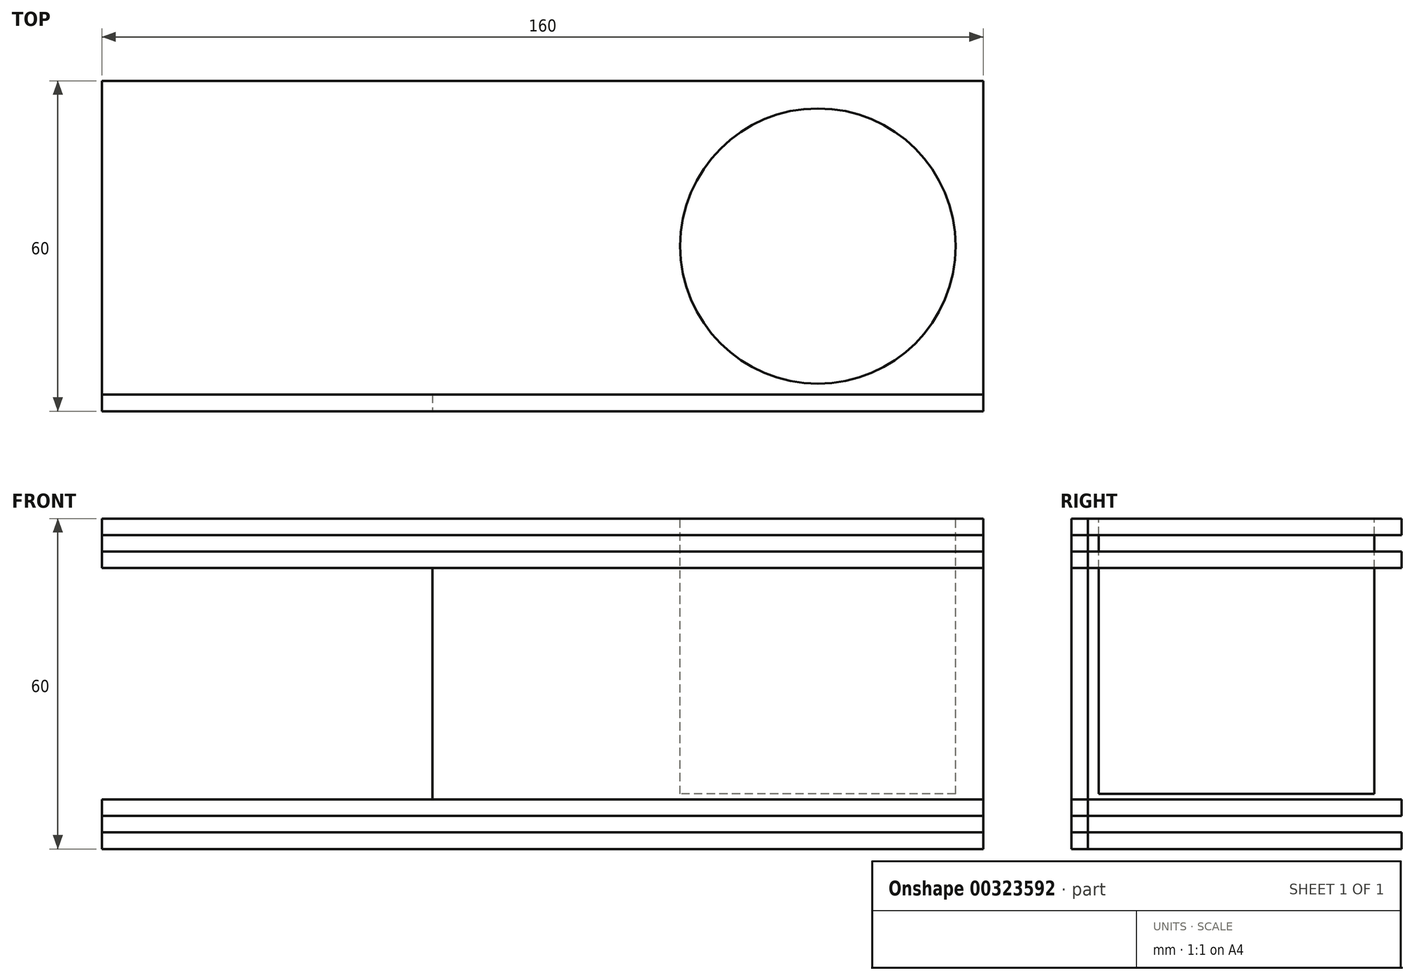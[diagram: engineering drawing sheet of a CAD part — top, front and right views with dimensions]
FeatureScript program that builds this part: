
annotation { "Feature Type Name" : "Feature", "Feature Type Description" : "" }
export const myFeature = defineFeature(function(context is Context, id is Id, definition is map)
    precondition{}
    {
        {
            assignVariable(context, id + "F0", {"name" : "WT", "anyValue" : 3});
        }
        {
            assignVariable(context, id + "F1", {"name" : "BS", "anyValue" : 60});
        }
        {
            assignVariable(context, id + "F2", {"name" : "Rig", "anyValue" : 100});
        }
        {
            var Q0;
            Q0=qCreatedBy(makeId("Top.planeOp"),FACE);
            var sketch = newSketch(context, id + "F3", { "sketchPlane" : qUnion([Q0])});
            skLineSegment(sketch, "E0.bottom", {"start": v(-30, 30) * mm, "end": v(30, 30) * mm});
            skLineSegment(sketch, "E0.top", {"start": v(-30, -30) * mm, "end": v(30, -30) * mm});
            skLineSegment(sketch, "E0.left", {"start": v(-30, 30) * mm, "end": v(-30, -30) * mm});
            skLineSegment(sketch, "E0.right", {"start": v(30, 30) * mm, "end": v(30, -30) * mm});
            skPoint(sketch, "E0.middle", {"position": v(0, 0) * mm});
            skLineSegment(sketch, "E1.bottom", {"start": v(-30, 30) * mm, "end": v(130, 30) * mm});
            skLineSegment(sketch, "E1.top", {"start": v(-30, -30) * mm, "end": v(130, -30) * mm});
            skLineSegment(sketch, "E1.right", {"start": v(130, 30) * mm, "end": v(130, -30) * mm});
            skLineSegment(sketch, "E2", {"start": v(-30, 30) * mm, "end": v(130, -30) * mm, "construction": true});
            skLineSegment(sketch, "E3", {"start": v(50, 0) * mm, "end": v(-30, 0) * mm, "construction": true});
            skPoint(sketch, "E3.endSnap0", {"position": v(-30, 0) * mm});
            skLineSegment(sketch, "E4", {"start": v(50, 0) * mm, "end": v(130, 0) * mm, "construction": true});
            skCircle(sketch, "E5", {"center": v(100, 0) * mm, "radius": 25 * mm});
            skLineSegment(sketch, "E6", {"start": v(130, 27) * mm, "end": v(30, 27) * mm});
            skLineSegment(sketch, "E7.MirrorCS", {"start": v(130, -27) * mm, "end": v(30, -27) * mm});
            skLineSegment(sketch, "E8", {"start": v(33, -27) * mm, "end": v(33, 27) * mm});
            skLineSegment(sketch, "E9", {"start": v(127, 27) * mm, "end": v(127, -27) * mm});
            skLineSegment(sketch, "E10", {"start": v(-27, 0) * mm, "end": v(-27, 27) * mm});
            skLineSegment(sketch, "E11", {"start": v(-27, 27) * mm, "end": v(27, 27) * mm});
            skLineSegment(sketch, "E12", {"start": v(27, 27) * mm, "end": v(27, 0) * mm});
            skLineSegment(sketch, "E13.MirrorCS", {"start": v(-27, 0) * mm, "end": v(-27, -27) * mm});
            skLineSegment(sketch, "E14.MirrorCS", {"start": v(-27, -27) * mm, "end": v(27, -27) * mm});
            skLineSegment(sketch, "E15.MirrorCS", {"start": v(27, -27) * mm, "end": v(27, 0) * mm});
            skSolve(sketch);
        }
        {
            var Q0;
            Q0=sQuery(id+"F3.wireOp",EDGE,"E1.right");
            cPlane(context, id + "F4", {"entities" : qUnion([Q0]), "cplaneType" : CPlaneType.LINE_ANGLE, "offset" : 25 * mm, "angle" : 90 * degree, "width" : 150 * mm, "height" : 150 * mm});
        }
        {
            var Q0;
            Q0=qCreatedBy(id+"F4.planeOp",FACE);
            var sketch = newSketch(context, id + "F5", { "sketchPlane" : qUnion([Q0])});
            skLineSegment(sketch, "E16.0", {"start": v(30, 0) * mm, "end": v(-30, 0) * mm});
            skLineSegment(sketch, "E17", {"start": v(-30, 0) * mm, "end": v(-30, -60) * mm});
            skLineSegment(sketch, "E18", {"start": v(-30, -60) * mm, "end": v(30, -60) * mm});
            skLineSegment(sketch, "E19", {"start": v(30, -60) * mm, "end": v(30, 0) * mm});
            skSolve(sketch);
        }
        {
            var Q0;
            Q0=sQuery(id+"F3.wireOp",EDGE,"E0.right");
            cPlane(context, id + "F6", {"entities" : qUnion([Q0]), "cplaneType" : CPlaneType.LINE_ANGLE, "offset" : 25 * mm, "angle" : 90 * degree, "width" : 150 * mm, "height" : 150 * mm});
        }
        {
            var Q0;
            Q0=qCreatedBy(id+"F6.planeOp",FACE);
            var sketch = newSketch(context, id + "F7", { "sketchPlane" : qUnion([Q0])});
            skLineSegment(sketch, "E20.0", {"start": v(30, 0) * mm, "end": v(-30, 0) * mm});
            skLineSegment(sketch, "E21.bottom", {"start": v(-30, -9) * mm, "end": v(30, -9) * mm});
            skLineSegment(sketch, "E21.top", {"start": v(-30, 0) * mm, "end": v(30, 0) * mm});
            skLineSegment(sketch, "E21.left", {"start": v(-30, -9) * mm, "end": v(-30, 0) * mm});
            skLineSegment(sketch, "E21.right", {"start": v(30, -9) * mm, "end": v(30, 0) * mm});
            skPoint(sketch, "E21.middle", {"position": v(0, -4.5) * mm});
            skLineSegment(sketch, "E22.bottom", {"start": v(-27, -3) * mm, "end": v(27, -3) * mm});
            skLineSegment(sketch, "E22.top", {"start": v(-27, -6) * mm, "end": v(27, -6) * mm});
            skLineSegment(sketch, "E22.left", {"start": v(-27, -3) * mm, "end": v(-27, -6) * mm});
            skLineSegment(sketch, "E22.right", {"start": v(27, -3) * mm, "end": v(27, -6) * mm});
            skLineSegment(sketch, "E23.0", {"start": v(-30, 0) * mm, "end": v(-30, -60) * mm});
            skLineSegment(sketch, "E24.0", {"start": v(-30, -60) * mm, "end": v(30, -60) * mm});
            skLineSegment(sketch, "E25", {"start": v(30, -60) * mm, "end": v(-30, 0) * mm, "construction": true});
            skLineSegment(sketch, "E26", {"start": v(0, -30) * mm, "end": v(-30, -30) * mm, "construction": true});
            skLineSegment(sketch, "E27.MirrorCS", {"start": v(-30, -51) * mm, "end": v(30, -51) * mm});
            skLineSegment(sketch, "E28.MirrorCS", {"start": v(-27, -54) * mm, "end": v(27, -54) * mm});
            skLineSegment(sketch, "E29.MirrorCS", {"start": v(-27, -57) * mm, "end": v(27, -57) * mm});
            skLineSegment(sketch, "E30.MirrorCS", {"start": v(-27, -57) * mm, "end": v(-27, -54) * mm});
            skLineSegment(sketch, "E31.MirrorCS", {"start": v(27, -57) * mm, "end": v(27, -54) * mm});
            skLineSegment(sketch, "E32.MirrorCS", {"start": v(30, -51) * mm, "end": v(30, -60) * mm});
            skLineSegment(sketch, "E33.0", {"start": v(30, -60) * mm, "end": v(30, 0) * mm});
            skLineSegment(sketch, "E34", {"start": v(-27, 0) * mm, "end": v(-27, -60) * mm});
            skLineSegment(sketch, "E35", {"start": v(27, 0) * mm, "end": v(27, -60) * mm});
            skLineSegment(sketch, "E36", {"start": v(27, -6) * mm, "end": v(30, -6) * mm});
            skPoint(sketch, "E36.endSnap0", {"position": v(30, -4.5) * mm});
            skLineSegment(sketch, "E37", {"start": v(-27, -6) * mm, "end": v(-30, -6) * mm});
            skLineSegment(sketch, "E38", {"start": v(27, -54) * mm, "end": v(30, -54) * mm});
            skLineSegment(sketch, "E39", {"start": v(-27, -54) * mm, "end": v(-30, -54) * mm});
            skLineSegment(sketch, "E40", {"start": v(-27, -57) * mm, "end": v(-30, -57) * mm});
            skLineSegment(sketch, "E41", {"start": v(27, -57) * mm, "end": v(30, -57) * mm});
            skSolve(sketch);
        }
        {
            var Q0;
            Q0=qCreatedBy(id+"F6.planeOp",FACE);
            var sketch = newSketch(context, id + "F8", { "sketchPlane" : qUnion([Q0])});
            skLineSegment(sketch, "E42.0", {"start": v(-30, 0) * mm, "end": v(-30, -60) * mm});
            skLineSegment(sketch, "E42.1", {"start": v(-30, 0) * mm, "end": v(30, 0) * mm});
            skLineSegment(sketch, "E42.2", {"start": v(30, -60) * mm, "end": v(30, 0) * mm});
            skLineSegment(sketch, "E42.3", {"start": v(-30, -60) * mm, "end": v(30, -60) * mm});
            skLineSegment(sketch, "E42.4", {"start": v(-27, -6) * mm, "end": v(27, -6) * mm});
            skLineSegment(sketch, "E42.5", {"start": v(-27, -3) * mm, "end": v(27, -3) * mm});
            skLineSegment(sketch, "E42.6", {"start": v(-27, -54) * mm, "end": v(27, -54) * mm});
            skLineSegment(sketch, "E42.7", {"start": v(-27, -57) * mm, "end": v(27, -57) * mm});
            skLineSegment(sketch, "E43", {"start": v(-27, -57) * mm, "end": v(-27, -54) * mm});
            skLineSegment(sketch, "E44", {"start": v(27, -57) * mm, "end": v(27, -54) * mm});
            skLineSegment(sketch, "E45", {"start": v(27, -6) * mm, "end": v(27, -3) * mm});
            skLineSegment(sketch, "E46", {"start": v(-27, -6) * mm, "end": v(-27, -3) * mm});
            skSolve(sketch);
        }
        {
            var Q0;
            Q0=qCreatedBy(makeId("Top.planeOp"),FACE);
            var sketch = newSketch(context, id + "F9", { "sketchPlane" : qUnion([Q0])});
            skLineSegment(sketch, "E47.0", {"start": v(-30, 30) * mm, "end": v(-30, -30) * mm});
            skLineSegment(sketch, "E48.0", {"start": v(-30, -30) * mm, "end": v(130, -30) * mm});
            skLineSegment(sketch, "E49.0", {"start": v(-30, 30) * mm, "end": v(130, 30) * mm});
            skLineSegment(sketch, "E50.0", {"start": v(130, 30) * mm, "end": v(130, -30) * mm});
            skSolve(sketch);
        }
        {
            var Q0;
            Q0=sQuery(id+"F3.wireOp",EDGE,"E1.top");
            cPlane(context, id + "F10", {"entities" : qUnion([Q0]), "cplaneType" : CPlaneType.LINE_ANGLE, "offset" : 25 * mm, "angle" : 0 * degree, "width" : 150 * mm, "height" : 150 * mm});
        }
        {
            var Q0;
            Q0=qCreatedBy(id+"F10.planeOp",FACE);
            var sketch = newSketch(context, id + "F11", { "sketchPlane" : qUnion([Q0])});
            skLineSegment(sketch, "E51.0", {"start": v(30, 0) * mm, "end": v(-130, 0) * mm});
            skLineSegment(sketch, "E52.0", {"start": v(-130, 0) * mm, "end": v(-130, -60) * mm});
            skLineSegment(sketch, "E53", {"start": v(30, -60) * mm, "end": v(-130, -60) * mm});
            skLineSegment(sketch, "E54.0", {"start": v(-30, 0) * mm, "end": v(-30, -60) * mm});
            skLineSegment(sketch, "E55", {"start": v(-30, -9) * mm, "end": v(30, -9) * mm});
            skLineSegment(sketch, "E56", {"start": v(30, -9) * mm, "end": v(30, 0) * mm});
            skLineSegment(sketch, "E57", {"start": v(30, -60) * mm, "end": v(30, -51) * mm});
            skLineSegment(sketch, "E58", {"start": v(30, -51) * mm, "end": v(-30, -51) * mm});
            skSolve(sketch);
        }
        {
            var Q0;
            Q0=makeQuery(id+"F3.imprint","IMPRINT",FACE,{"disambiguationData":[TD([[makeQuery(id+"F3.imprint","IMPRINT",EDGE,{"derivedFrom":sQuery(id+"F3.wireOp",EDGE,"E5")}),1.0]])]});
            extrude(context, id + "F12", {"entities" : qUnion([Q0]), "oppositeDirection" : true, "depth" : 50 * mm});
        }
        {
            var Q0;
            Q0=makeQuery(id+"F9.imprint","IMPRINT",FACE,{"disambiguationData":[TD([[makeQuery(id+"F9.imprint","IMPRINT",EDGE,{"derivedFrom":sQuery(id+"F9.wireOp",EDGE,"E47.0")}),1.0]])]});
            extrude(context, id + "F13", {"entities" : qUnion([Q0]), "oppositeDirection" : true, "depth" : (getVariable(context, 'WT')) * mm});
        }
        {
            var Q0;
            {var subQ5=sQuery(id+"F7.wireOp",EDGE,"E22.top");Q0=makeQuery(id+"F7.imprint","IMPRINT",FACE,{"disambiguationData":[TD([[makeQuery(id+"F7.imprint","IMPRINT",EDGE,{"derivedFrom":subQ5}),-1.0]])]});}
            var Q1;
            {var subQ5=sQuery(id+"F7.wireOp",EDGE,"E36");Q1=makeQuery(id+"F7.imprint","IMPRINT",FACE,{"disambiguationData":[TD([[makeQuery(id+"F7.imprint","IMPRINT",EDGE,{"derivedFrom":subQ5}),-1.0]])]});}
            var Q2;
            {var subQ5=sQuery(id+"F7.wireOp",EDGE,"E37");Q2=makeQuery(id+"F7.imprint","IMPRINT",FACE,{"disambiguationData":[TD([[makeQuery(id+"F7.imprint","IMPRINT",EDGE,{"derivedFrom":subQ5}),1.0]])]});}
            extrude(context, id + "F14", {"entities" : qUnion([Q0, Q1, Q2]), "depth" : (getVariable(context, 'Rig')) * mm, "hasSecondDirection" : true, "secondDirectionOppositeDirection" : true, "secondDirectionDepth" : (getVariable(context, 'BS')) * mm});
        }
        {
            var Q0;
            {var subQ5=sQuery(id+"F7.wireOp",EDGE,"E28.MirrorCS");Q0=makeQuery(id+"F7.imprint","IMPRINT",FACE,{"disambiguationData":[TD([[makeQuery(id+"F7.imprint","IMPRINT",EDGE,{"derivedFrom":subQ5}),1.0]])]});}
            var Q1;
            {var subQ5=sQuery(id+"F7.wireOp",EDGE,"E38");Q1=makeQuery(id+"F7.imprint","IMPRINT",FACE,{"disambiguationData":[TD([[makeQuery(id+"F7.imprint","IMPRINT",EDGE,{"derivedFrom":subQ5}),1.0]])]});}
            var Q2;
            {var subQ3=sQuery(id+"F7.wireOp",EDGE,"E39");Q2=makeQuery(id+"F7.imprint","IMPRINT",FACE,{"disambiguationData":[TD([[makeQuery(id+"F7.imprint","IMPRINT",EDGE,{"derivedFrom":subQ3}),-1.0]])]});}
            extrude(context, id + "F15", {"entities" : qUnion([Q0, Q1, Q2]), "depth" : (getVariable(context, 'Rig')) * mm, "hasSecondDirection" : true, "secondDirectionOppositeDirection" : true, "secondDirectionDepth" : (getVariable(context, 'BS')) * mm});
        }
        {
            var Q0;
            {var subQ0=sQuery(id+"F7.wireOp",EDGE,"E29.MirrorCS");Q0=makeQuery(id+"F7.imprint","IMPRINT",FACE,{"disambiguationData":[TD([[makeQuery(id+"F7.imprint","IMPRINT",EDGE,{"derivedFrom":subQ0}),-1.0]])]});}
            var Q1;
            {var subQ5=sQuery(id+"F7.wireOp",EDGE,"E41");Q1=makeQuery(id+"F7.imprint","IMPRINT",FACE,{"disambiguationData":[TD([[makeQuery(id+"F7.imprint","IMPRINT",EDGE,{"derivedFrom":subQ5}),-1.0]])]});}
            var Q2;
            {var subQ3=sQuery(id+"F7.wireOp",EDGE,"E40");Q2=makeQuery(id+"F7.imprint","IMPRINT",FACE,{"disambiguationData":[TD([[makeQuery(id+"F7.imprint","IMPRINT",EDGE,{"derivedFrom":subQ3}),1.0]])]});}
            extrude(context, id + "F16", {"entities" : qUnion([Q0, Q1, Q2]), "depth" : (getVariable(context, 'Rig')) * mm, "hasSecondDirection" : true, "secondDirectionOppositeDirection" : true, "secondDirectionDepth" : (getVariable(context, 'BS')) * mm});
        }
        {
            var Q0;
            {var subQ5=sQuery(id+"F11.wireOp",EDGE,"E52.0");Q0=makeQuery(id+"F11.imprint","IMPRINT",FACE,{"disambiguationData":[TD([[makeQuery(id+"F11.imprint","IMPRINT",EDGE,{"derivedFrom":subQ5}),1.0]])]});}
            var Q1;
            {var subQ4=sQuery(id+"F11.wireOp",EDGE,"E55");Q1=makeQuery(id+"F11.imprint","IMPRINT",FACE,{"disambiguationData":[TD([[makeQuery(id+"F11.imprint","IMPRINT",EDGE,{"derivedFrom":subQ4}),1.0]])]});}
            var Q2;
            {var subQ0=sQuery(id+"F11.wireOp",EDGE,"E57");Q2=makeQuery(id+"F11.imprint","IMPRINT",FACE,{"disambiguationData":[TD([[makeQuery(id+"F11.imprint","IMPRINT",EDGE,{"derivedFrom":subQ0}),1.0]])]});}
            extrude(context, id + "F17", {"entities" : qUnion([Q0, Q1, Q2]), "depth" : (getVariable(context, 'WT')) * mm});
        }
    });
